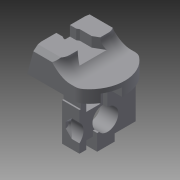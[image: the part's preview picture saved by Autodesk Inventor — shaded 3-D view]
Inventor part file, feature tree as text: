
AUTODESK INVENTOR PART (.ipt)
format: ipt  version: 2014 SP1 (Build 180222100, 222)  size: 392,192 bytes
history: native  units: in
note: dims shown in document units (in); Inventor stores cm internally (conversion verified against a paired STEP export)
features: sketch x11, projected_geometry x10, extrude x9, other x4, reference x4, revolve x1
ambient origin geometry x8: Origin, YZ Plane, XZ Plane, XY Plane, X Axis, Y Axis, Z Axis, Center Point
bodies: Solid1 (feature_tree)
feature tree (39):
  other  "Slide"
  sketch  "Sketch1"  dims[d0=0.3937in d1=0.0485in]
  extrude  "Extrusion1"  Depth=0.3937in
  extrude  "Extrusion3"  Depth=0.37in TaperAngle=0.0deg
  extrude  "Extrusion4"  Depth=0.1345in
  extrude  "Extrusion5"  Depth=0.0485in TaperAngle=0.0deg
  extrude  "Extrusion6"  Depth=0.079in TaperAngle=0.0deg
  extrude  "Extrusion7"  Depth=0.08in
  extrude  "Extrusion8"  Depth=0.2765in TaperAngle=0.0deg
  extrude  "Extrusion9"  Depth=0.0299in
  sketch  "Sketch16"  dims[d40=45.0deg d41=0.04in]
  other  "Work Axis3"
  revolve  "Revolution3"  [1 undecoded]
  extrude  "Extrusion10"  Depth=0.04in
  other  "Rear Sight::Slide"
  other  "TaggingFeature1"
  sketch  "Sketch2"  dims[d2=1.0in d3=0.0in d6=0.37in d7=0.0in]
  reference  "Reference1"
  sketch  "Sketch4"  dims[d9=0.235in d10=0.1345in]
  reference  "Reference2"
  sketch  "Sketch5"  dims[d12=0.1in d13=0.0485in d14=0.0in]
  projected_geometry  "Projected Loop1"
  sketch  "Sketch6"  dims[d15=0.042in d16=0.0in d18=0.079in d19=0.0in]
  projected_geometry  "Projected Loop2"
  sketch  "Sketch7"  dims[d20=0.2765in d21=0.0in d22=0.08in]
  projected_geometry  "Projected Loop3"
  sketch  "Sketch8"  dims[d23=0.5915in d24=0.2765in d25=0.0in]
  sketch  "Sketch9"  dims[d26=0.004in d32=0.0299in]
  projected_geometry  "Projected Loop4"
  projected_geometry  "Projected Loop5"
  reference  "Reference3"
  reference  "Reference4"
  sketch  "Sketch13"  dims[d33=0.2in d34=0.0855in d35=0.0in]
  projected_geometry  "Projected Loop8"
  projected_geometry  "Projected Loop10"
  sketch  "Sketch17"  dims[d42=90.0deg d43=0.0855in d44=0.0in]
  projected_geometry  "Projected Loop11"
  projected_geometry  "Project Cut Edges1"
  projected_geometry  "Project Cut Edges3"
note: 1 required parameter value undecoded (feature->parameter linkage not recoverable at this tier; creation-order binding heuristic only, values carry confidence <= 0.55)
